# Revit family: 1183xxx Messina
name_source: partatom
category: Lighting Fixtures
revit_build: Autodesk Revit 2018 (Build: 20170223_1515(x64)
units: mm (PartAtom-declared; Revit-internal decimal feet)

## family parameters
Always vertical = Yes
Cut with Voids When Loaded = No
Host = Wall
Light Source = No
OmniClass Number = 23.80.70.00
OmniClass Title = Lighting
Part Type = Normal
Room Calculation Point = No
Round Connector Dimension = Use Diameter
Shared = No

## types (6) — shared parameters
ADA compliant = Yes
Dimmable = Yes
Dimming Method = Lamp Dependent
Driver Included = Not Applicable
Driver Required = No
Efficacy (lm/w) = Lamp Dependent
Electrical Class = 1
Lamp = Incandescent
Light Source Fixed = No
Location / IP Rating = Wet
Main Material = Metal - Stainless steel
Manufacturer = Astro Lighting Ltd
Manufacturer URL - Europe and Rest of World = www.astrolighting.com
Manufacturer URL - North America = us.astrolighting.com
Power (Watts) = Lamp Dependent
Product CCT = Lamp Dependent
Product CRI = Lamp Dependent
Product Dimensions (MM) = 350x160x100
Product Location = Exterior
Product Weight (KG) = 5.72
URL = www.astrolighting.com

## per-type parameters (varying)
| type | Main Finish | Product Name | Product URL |
| 1183014 | Textured Black | Messina Frosted | https://us.astrolighting.com |
| 1183015 | Bronze | Messina | https://us.astrolighting.com |
| 1183012 | Bronze | Messina Frosted | https://us.astrolighting.com |
| 1183017 | Textured Black | Messina | https://us.astrolighting.com |
| 1183013 | Polished Nickel | Messina Frosted |  |
| 1183016 | Polished Nickel | Messina |  |

note: column(s) folded — value = type name in every type: Product SKU

## geometry (parser evidence)
native form markers: Sweep x2
no freeform markers — native parametric forms only
